FCSTD DOCUMENT  (FreeCAD 0.15R4671 (Git))
Label: 2xBearingBase
License: All rights reserved
LicenseURL: http://en.wikipedia.org/wiki/All_rights_reserved
objects: Sketcher::SketchObject×10, Mesh::Feature×8, PartDesign::Pocket×6, Part::Feature×3, PartDesign::Pad×3
note: 31 computed .brp shape members not serialized (recipe doc carries the construction recipe); baked Part::Feature solids carry a one-line shape summary decoded from their .brp

FEATURE [Part::Feature] LM8UU_8mm_Linear_Bearing
  shape: bbox 24 x 15 x 15 mm, 34 faces (baked)
FEATURE [Part::Feature] LM8UU_8mm_Linear_Bearing001
  Placement = pos=(28,0,0) rot=(0,0,1;0rad)
  shape: bbox 24 x 15 x 15 mm, 34 faces (baked)
FEATURE [Sketcher::SketchObject] Sketch
  sketch-geometry (4):
    g0: LineSegment StartX=-2 StartY=-15 StartZ=0 EndX=54 EndY=-15 EndZ=0
    g1: LineSegment StartX=54 StartY=-15 StartZ=0 EndX=54 EndY=15 EndZ=0
    g2: LineSegment StartX=54 StartY=15 StartZ=0 EndX=-2 EndY=15 EndZ=0
    g3: LineSegment StartX=-2 StartY=15 StartZ=0 EndX=-2 EndY=-15 EndZ=0
  constraints (8):
    c: Coincident(g0,g1)
    c: Coincident(g1,g2)
    c: Coincident(g2,g3)
    c: Coincident(g3,g0)
    c: Horizontal(g0)
    c: Horizontal(g2)
    c: Vertical(g1)
    c: Vertical(g3)
FEATURE [PartDesign::Pad] Pad
  Length = 9
  Length2 = 100
  Sketch = -> Sketch
  Type = 0
FEATURE [Sketcher::SketchObject] Sketch001
  Placement = pos=(-2,0,0) rot=(0.57735,-0.57735,-0.57735;2.0944rad)
  Support = -> Pad [Face4]
  sketch-geometry (1):
    g0: Circle CenterX=0 CenterY=0 CenterZ=0 NormalX=0 NormalY=0 NormalZ=1 Radius=7.75
  constraints (2):
    c: Coincident(g0,g-1)
    c: Radius(g0) = 7.75
FEATURE [PartDesign::Pocket] Pocket
  Length = 26.25
  Sketch = -> Sketch001
  Type = 0
FEATURE [Sketcher::SketchObject] Sketch002
  Placement = pos=(54,0,0) rot=(0.57735,0.57735,0.57735;2.0944rad)
  Support = -> Pocket [Face3]
  sketch-geometry (1):
    g0: Circle CenterX=0 CenterY=0 CenterZ=0 NormalX=0 NormalY=0 NormalZ=1 Radius=7.75
  constraints (2):
    c: Coincident(g0,g-1)
    c: Radius(g0) = 7.75
FEATURE [PartDesign::Pocket] Pocket001
  Length = 26.25
  Sketch = -> Sketch002
  Type = 0
FEATURE [Sketcher::SketchObject] Sketch003
  Placement = pos=(54,0,0) rot=(0.57735,0.57735,0.57735;2.0944rad)
  Support = -> Pocket001 [Face3]
  sketch-geometry (2):
    g0: ArcOfCircle CenterX=0 CenterY=0 CenterZ=0 NormalX=0 NormalY=0 NormalZ=1 Radius=8 StartAngle=0 EndAngle=3.14159
    g1: LineSegment StartX=-8 StartY=0 StartZ=0 EndX=8 EndY=0 EndZ=0
  constraints (3):
    c: Coincident(g1,g0)
    c: Coincident(g1,g0)
    c: Horizontal(g1)
FEATURE [PartDesign::Pad] Pad001
  Length = 1.75
  Length2 = 100
  Reversed = true
  Sketch = -> Sketch003
  Type = 0
FEATURE [Sketcher::SketchObject] Sketch004
  Placement = pos=(-2,0,0) rot=(0.57735,-0.57735,-0.57735;2.0944rad)
  Support = -> Pad001 [Face2]
  sketch-geometry (2):
    g0: ArcOfCircle CenterX=0 CenterY=0 CenterZ=0 NormalX=0 NormalY=0 NormalZ=1 Radius=8 StartAngle=0 EndAngle=3.14159
    g1: LineSegment StartX=-8 StartY=0 StartZ=0 EndX=8 EndY=0 EndZ=0
  constraints (5):
    c: Coincident(g0,g-1)
    c: PointOnObject(g0,g-1)
    c: PointOnObject(g0,g-1)
    c: Coincident(g1,g0)
    c: Coincident(g1,g0)
FEATURE [PartDesign::Pad] Pad002
  Length = 1.75
  Length2 = 100
  Reversed = true
  Sketch = -> Sketch004
  Type = 0
FEATURE [Sketcher::SketchObject] Sketch005
  Placement = pos=(-2,0,0) rot=(0.57735,-0.57735,-0.57735;2.0944rad)
  Support = -> Pad002 [Face5]
  sketch-geometry (1):
    g0: Circle CenterX=0 CenterY=0 CenterZ=0 NormalX=0 NormalY=0 NormalZ=1 Radius=6.5
  constraints (1):
    c: Radius(g0) = 6.5
FEATURE [PartDesign::Pocket] Pocket002
  Length = 5
  Sketch = -> Sketch005
  Type = 1
FEATURE [Mesh::Feature] SocketHeadCapScrew_M3x008  label="SocketHeadCapScrew_M3x019"
  Placement = pos=(20,21,-113) rot=(0,0,1;0rad)
FEATURE [Mesh::Feature] SocketHeadCapScrew_M3x009  label="SocketHeadCapScrew_M3x020"
  Placement = pos=(48,21,-113) rot=(0,0,1;0rad)
FEATURE [Mesh::Feature] SocketHeadCapScrew_M3x011  label="SocketHeadCapScrew_M3x016"
  Placement = pos=(20,-1,-113) rot=(0,0,1;0rad)
FEATURE [Mesh::Feature] SocketHeadCapScrew_M3x012  label="SocketHeadCapScrew_M3x017"
  Placement = pos=(48,-1,-113) rot=(0,0,1;0rad)
FEATURE [Sketcher::SketchObject] Sketch006
  Placement = pos=(0,0,0) rot=(1,0,0;3.14159rad)
  Support = -> Pocket002 [Face4]
  sketch-geometry (4):
    g0: Circle CenterX=12 CenterY=11 CenterZ=0 NormalX=0 NormalY=0 NormalZ=1 Radius=1.8
    g1: Circle CenterX=12 CenterY=-11 CenterZ=0 NormalX=0 NormalY=0 NormalZ=1 Radius=1.8
    g2: Circle CenterX=40 CenterY=11 CenterZ=0 NormalX=0 NormalY=0 NormalZ=1 Radius=1.8
    g3: Circle CenterX=40 CenterY=-11 CenterZ=0 NormalX=0 NormalY=0 NormalZ=1 Radius=1.8
  constraints (4):
    c: Radius(g0) = 1.8
    c: Radius(g1) = 1.8
    c: Radius(g2) = 1.8
    c: Radius(g3) = 1.8
FEATURE [PartDesign::Pocket] Pocket003
  Length = 5
  Sketch = -> Sketch006
  Type = 1
FEATURE [Sketcher::SketchObject] Sketch007
  Placement = pos=(0,0,9) rot=(0,0,1;0rad)
  Support = -> Pocket003 [Face5]
  sketch-geometry (28):
    g0: LineSegment StartX=15.5 StartY=11 StartZ=0 EndX=13.75 EndY=14.0311 EndZ=0
    g1: LineSegment StartX=13.75 StartY=14.0311 StartZ=0 EndX=10.25 EndY=14.0311 EndZ=0
    g2: LineSegment StartX=10.25 StartY=14.0311 StartZ=0 EndX=8.5 EndY=11 EndZ=0
    g3: LineSegment StartX=8.5 StartY=11 StartZ=0 EndX=10.25 EndY=7.96891 EndZ=0
    g4: LineSegment StartX=10.25 StartY=7.96891 StartZ=0 EndX=13.75 EndY=7.96891 EndZ=0
    g5: LineSegment StartX=13.75 StartY=7.96891 StartZ=0 EndX=15.5 EndY=11 EndZ=0
    g6: Circle [constr] CenterX=12 CenterY=11 CenterZ=0 NormalX=0 NormalY=0 NormalZ=1 Radius=3.5
    g7: LineSegment StartX=43.5 StartY=11 StartZ=0 EndX=41.75 EndY=14.0311 EndZ=0
    g8: LineSegment StartX=41.75 StartY=14.0311 StartZ=0 EndX=38.25 EndY=14.0311 EndZ=0
    g9: LineSegment StartX=38.25 StartY=14.0311 StartZ=0 EndX=36.5 EndY=11 EndZ=0
    g10: LineSegment StartX=36.5 StartY=11 StartZ=0 EndX=38.25 EndY=7.96891 EndZ=0
    g11: LineSegment StartX=38.25 StartY=7.96891 StartZ=0 EndX=41.75 EndY=7.96891 EndZ=0
    g12: LineSegment StartX=41.75 StartY=7.96891 StartZ=0 EndX=43.5 EndY=11 EndZ=0
    g13: Circle [constr] CenterX=40 CenterY=11 CenterZ=0 NormalX=0 NormalY=0 NormalZ=1 Radius=3.5
    g14: LineSegment StartX=43.5 StartY=-11 StartZ=0 EndX=41.75 EndY=-7.96891 EndZ=0
    g15: LineSegment StartX=41.75 StartY=-7.96891 StartZ=0 EndX=38.25 EndY=-7.96891 EndZ=0
    g16: LineSegment StartX=38.25 StartY=-7.96891 StartZ=0 EndX=36.5 EndY=-11 EndZ=0
    g17: LineSegment StartX=36.5 StartY=-11 StartZ=0 EndX=38.25 EndY=-14.0311 EndZ=0
    g18: LineSegment StartX=38.25 StartY=-14.0311 StartZ=0 EndX=41.75 EndY=-14.0311 EndZ=0
    g19: LineSegment StartX=41.75 StartY=-14.0311 StartZ=0 EndX=43.5 EndY=-11 EndZ=0
    g20: Circle [constr] CenterX=40 CenterY=-11 CenterZ=0 NormalX=0 NormalY=0 NormalZ=1 Radius=3.5
    g21: LineSegment StartX=15.5 StartY=-11 StartZ=0 EndX=13.75 EndY=-7.96891 EndZ=0
    g22: LineSegment StartX=13.75 StartY=-7.96891 StartZ=0 EndX=10.25 EndY=-7.96891 EndZ=0
    g23: LineSegment StartX=10.25 StartY=-7.96891 StartZ=0 EndX=8.5 EndY=-11 EndZ=0
    g24: LineSegment StartX=8.5 StartY=-11 StartZ=0 EndX=10.25 EndY=-14.0311 EndZ=0
    g25: LineSegment StartX=10.25 StartY=-14.0311 StartZ=0 EndX=13.75 EndY=-14.0311 EndZ=0
    g26: LineSegment StartX=13.75 StartY=-14.0311 StartZ=0 EndX=15.5 EndY=-11 EndZ=0
    g27: Circle [constr] CenterX=12 CenterY=-11 CenterZ=0 NormalX=0 NormalY=0 NormalZ=1 Radius=3.5
  constraints (56):
    c: Coincident(g0,g1)
    c: Coincident(g1,g2)
    c: Coincident(g2,g3)
    c: Coincident(g3,g4)
    c: Coincident(g4,g5)
    c: Coincident(g5,g0)
    c: Equal(g0, g1-g5) x5
    c: PointOnObject(g0,g6)
    c: PointOnObject(g1,g6)
    c: PointOnObject(g2,g6)
    c: PointOnObject(g3,g6)
    c: PointOnObject(g4,g6)
    c: PointOnObject(g5,g6)
    c: Horizontal(g4)
    c: Coincident(g7,g8)
    c: Coincident(g8,g9)
    c: Coincident(g9,g10)
    c: Coincident(g10,g11)
    c: Coincident(g11,g12)
    c: Coincident(g12,g7)
    c: Equal(g7, g8-g12) x5
    c: PointOnObject(g7,g13)
    c: PointOnObject(g8,g13)
    c: PointOnObject(g9,g13)
    c: PointOnObject(g10,g13)
    c: PointOnObject(g11,g13)
    c: PointOnObject(g12,g13)
    c: Horizontal(g11)
    c: Coincident(g14,g15)
    c: Coincident(g15,g16)
    c: Coincident(g16,g17)
    c: Coincident(g17,g18)
    c: Coincident(g18,g19)
    c: Coincident(g19,g14)
    c: Equal(g14, g15-g19) x5
    c: PointOnObject(g14,g20)
    c: PointOnObject(g15,g20)
    c: PointOnObject(g16,g20)
    c: PointOnObject(g17,g20)
    c: PointOnObject(g18,g20)
    c: PointOnObject(g19,g20)
    c: Horizontal(g18)
    c: Coincident(g21,g22)
    c: Coincident(g22,g23)
    c: Coincident(g23,g24)
    c: Coincident(g24,g25)
    c: Coincident(g25,g26)
    c: Coincident(g26,g21)
    c: Equal(g21, g22-g26) x5
    c: PointOnObject(g21,g27)
    c: PointOnObject(g22,g27)
    c: PointOnObject(g23,g27)
    c: PointOnObject(g24,g27)
    c: PointOnObject(g25,g27)
    c: PointOnObject(g26,g27)
    c: Horizontal(g25)
FEATURE [PartDesign::Pocket] Pocket004
  Length = 7
  Sketch = -> Sketch007
  Type = 0
FEATURE [Sketcher::SketchObject] Sketch008
  Placement = pos=(0,0,0) rot=(1,0,0;3.14159rad)
  Support = -> Pocket004 [Face4]
  sketch-geometry (16):
    g0: ArcOfCircle CenterX=12 CenterY=11 CenterZ=0 NormalX=0 NormalY=0 NormalZ=1 Radius=4 StartAngle=0 EndAngle=3.14159
    g1: ArcOfCircle CenterX=40 CenterY=11 CenterZ=0 NormalX=0 NormalY=0 NormalZ=1 Radius=4 StartAngle=0 EndAngle=3.14159
    g2: ArcOfCircle CenterX=40 CenterY=-11 CenterZ=0 NormalX=0 NormalY=0 NormalZ=1 Radius=4 StartAngle=3.14159 EndAngle=6.28319
    g3: ArcOfCircle CenterX=12 CenterY=-11 CenterZ=0 NormalX=0 NormalY=0 NormalZ=1 Radius=4 StartAngle=3.14159 EndAngle=6.28319
    g4: LineSegment StartX=-3 StartY=-11 StartZ=0 EndX=-3 EndY=-17 EndZ=0
    g5: LineSegment StartX=-3 StartY=-17 StartZ=0 EndX=55 EndY=-17 EndZ=0
    g6: LineSegment StartX=55 StartY=-17 StartZ=0 EndX=55 EndY=-11 EndZ=0
    g7: LineSegment StartX=55 StartY=-11 StartZ=0 EndX=44 EndY=-11 EndZ=0
    g8: LineSegment StartX=36 StartY=-11 StartZ=0 EndX=16 EndY=-11 EndZ=0
    g9: LineSegment StartX=8 StartY=-11 StartZ=0 EndX=-3 EndY=-11 EndZ=0
    g10: LineSegment StartX=36 StartY=11 StartZ=0 EndX=16 EndY=11 EndZ=0
    g11: LineSegment StartX=8 StartY=11 StartZ=0 EndX=-3 EndY=11 EndZ=0
    g12: LineSegment StartX=-3 StartY=11 StartZ=0 EndX=-3 EndY=17 EndZ=0
    g13: LineSegment StartX=-3 StartY=17 StartZ=0 EndX=55 EndY=17 EndZ=0
    g14: LineSegment StartX=55 StartY=17 StartZ=0 EndX=55 EndY=11 EndZ=0
    g15: LineSegment StartX=55 StartY=11 StartZ=0 EndX=44 EndY=11 EndZ=0
  constraints (27):
    c: Vertical(g4)
    c: Coincident(g4,g5)
    c: Horizontal(g5)
    c: Coincident(g5,g6)
    c: Vertical(g6)
    c: Coincident(g7,g6)
    c: Coincident(g7,g2)
    c: Horizontal(g7)
    c: Coincident(g8,g2)
    c: Coincident(g8,g3)
    c: Horizontal(g8)
    c: Coincident(g9,g3)
    c: Coincident(g9,g4)
    c: Horizontal(g9)
    c: Coincident(g10,g1)
    c: Coincident(g10,g0)
    c: Horizontal(g10)
    c: Coincident(g0,g11)
    c: Coincident(g11,g12)
    c: Vertical(g12)
    c: Coincident(g12,g13)
    c: Horizontal(g13)
    c: Coincident(g13,g14)
    c: Vertical(g14)
    c: Coincident(g14,g15)
    c: Coincident(g15,g1)
    c: Horizontal(g15)
FEATURE [Mesh::Feature] HexNutStyle1_M3
  Placement = pos=(13.3,15.15,-114.5) rot=(0,0,1;0.523599rad)
FEATURE [Mesh::Feature] HexNutStyle1_M
  Placement = pos=(41.3,15.15,-114.5) rot=(0,0,1;0.523599rad)
FEATURE [Mesh::Feature] HexNutStyle1_M004
  Placement = pos=(13.3,37.15,-114.5) rot=(0,0,1;0.523599rad)
FEATURE [Mesh::Feature] HexNutStyle1_M005
  Placement = pos=(41.3,37.15,-114.5) rot=(0,0,1;0.523599rad)
FEATURE [Part::Feature] Part__Feature  label="2xBearingCap"
  shape: bbox 56 x 30 x 9 mm, 48 faces (baked)
FEATURE [Sketcher::SketchObject] Sketch009
  Placement = pos=(0,0,9) rot=(0,0,1;0rad)
  Support = -> Pocket004 [Face5]
  sketch-geometry (3):
    g0: Circle CenterX=26 CenterY=13 CenterZ=0 NormalX=0 NormalY=0 NormalZ=1 Radius=1.8
    g1: Circle CenterX=48 CenterY=-13 CenterZ=0 NormalX=0 NormalY=0 NormalZ=1 Radius=1.8
    g2: Circle CenterX=4 CenterY=-13 CenterZ=0 NormalX=0 NormalY=0 NormalZ=1 Radius=1.8
  constraints (3):
    c: Radius(g0) = 1.8
    c: Radius(g2) = 1.8
    c: Radius(g1) = 1.8
FEATURE [PartDesign::Pocket] Pocket005
  Length = 5
  Sketch = -> Sketch009
  Type = 1
